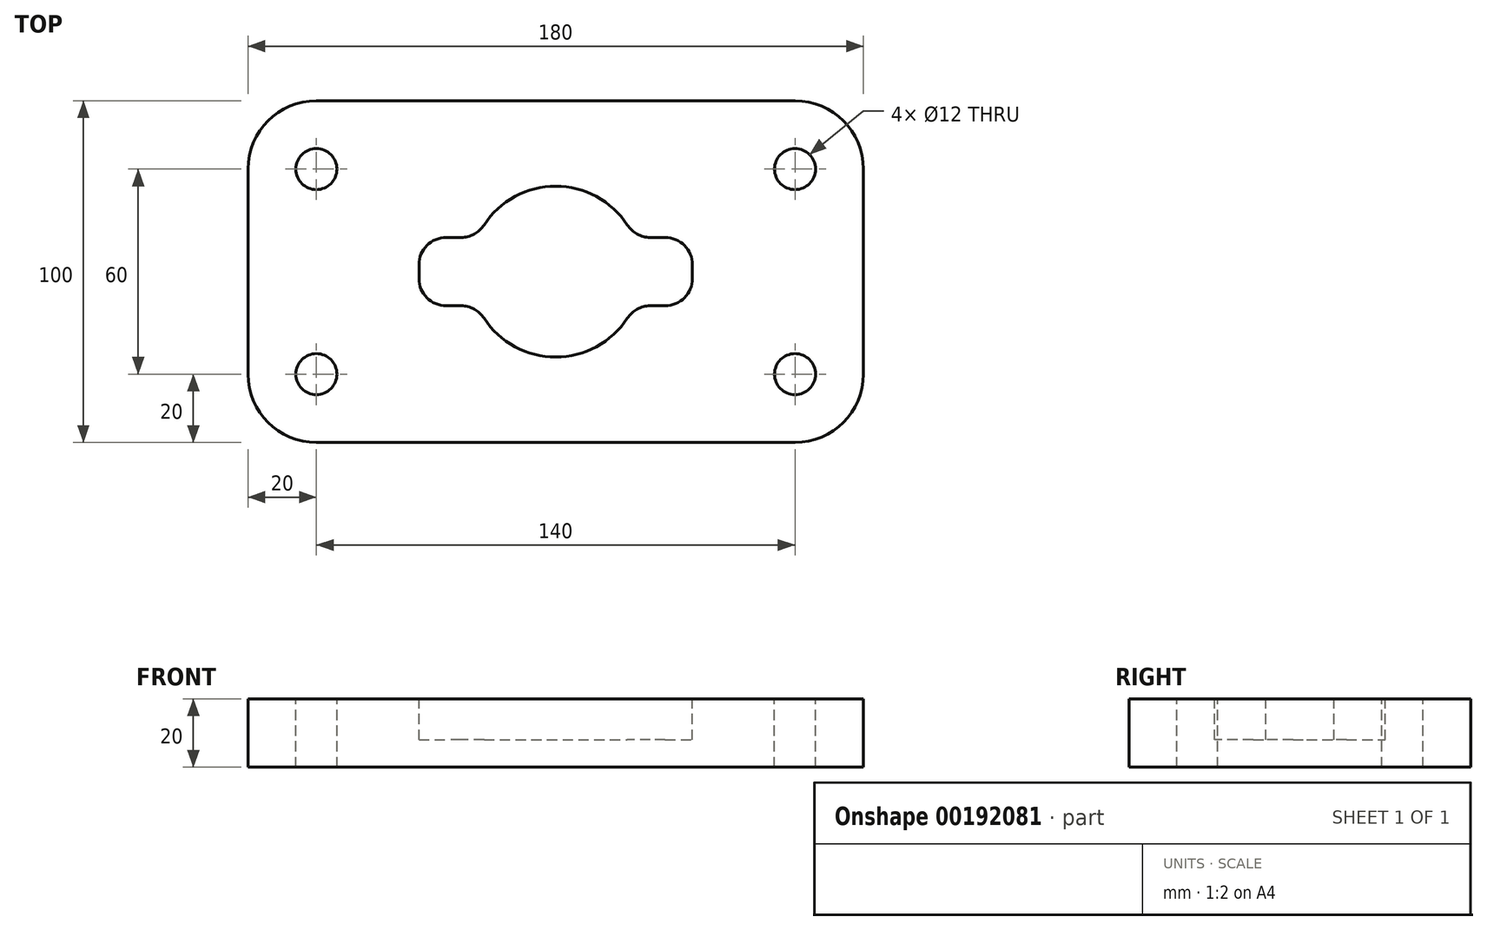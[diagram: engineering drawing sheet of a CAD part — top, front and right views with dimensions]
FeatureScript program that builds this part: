
annotation { "Feature Type Name" : "Feature", "Feature Type Description" : "" }
export const myFeature = defineFeature(function(context is Context, id is Id, definition is map)
    precondition{}
    {
        {
            var Q0;
            Q0=qCreatedBy(makeId("Top.planeOp"),FACE);
            var sketch = newSketch(context, id + "F0", { "sketchPlane" : qUnion([Q0])});
            skLineSegment(sketch, "E0.bottom", {"start": v(70, 50) * mm, "end": v(-70, 50) * mm});
            skLineSegment(sketch, "E0.top", {"start": v(70, -50) * mm, "end": v(-70, -50) * mm});
            skLineSegment(sketch, "E0.left", {"start": v(90, 30) * mm, "end": v(90, -30) * mm});
            skLineSegment(sketch, "E0.right", {"start": v(-90, 30) * mm, "end": v(-90, -30) * mm});
            skPoint(sketch, "E0.middle", {"position": v(0, 0) * mm});
            skPoint(sketch, "E1.visualSharp", {"position": v(-90, 50) * mm});
            skArc(sketch, "E1.filletArc", {"start": v(-70, 50) * mm, "mid": v(-84.14, 44.14) * mm, "end": v(-90, 30) * mm});
            skPoint(sketch, "E2.visualSharp", {"position": v(-90, -50) * mm});
            skArc(sketch, "E2.filletArc", {"start": v(-90, -30) * mm, "mid": v(-84.14, -44.14) * mm, "end": v(-70, -50) * mm});
            skPoint(sketch, "E3.visualSharp", {"position": v(90, -50) * mm});
            skArc(sketch, "E3.filletArc", {"start": v(70, -50) * mm, "mid": v(84.14, -44.14) * mm, "end": v(90, -30) * mm});
            skPoint(sketch, "E4.visualSharp", {"position": v(90, 50) * mm});
            skArc(sketch, "E4.filletArc", {"start": v(90, 30) * mm, "mid": v(84.14, 44.14) * mm, "end": v(70, 50) * mm});
            skSolve(sketch);
        }
        {
            var Q0;
            Q0 = qSketchRegion(id + "F0", true);
            extrude(context, id + "F1", {"entities" : qUnion([Q0]), "oppositeDirection" : true, "depth" : 20 * mm});
        }
        {
            var Q0;
            Q0=makeQuery(id+"F1.opExtrude","CAP_FACE",FACE,{"disambiguationData":[OSD([sQuery(id+"F0.wireOp",EDGE,"E0.bottom"),sQuery(id+"F0.wireOp",EDGE,"E0.top"),sQuery(id+"F0.wireOp",EDGE,"E0.left"),sQuery(id+"F0.wireOp",EDGE,"E0.right"),sQuery(id+"F0.wireOp",EDGE,"E1.filletArc"),sQuery(id+"F0.wireOp",EDGE,"E2.filletArc"),sQuery(id+"F0.wireOp",EDGE,"E3.filletArc"),sQuery(id+"F0.wireOp",EDGE,"E4.filletArc")])],"isStart":true});
            var sketch = newSketch(context, id + "F2", { "sketchPlane" : qUnion([Q0])});
            skCircle(sketch, "E5", {"center": v(70, 30) * mm, "radius": 6 * mm});
            skCircle(sketch, "E6", {"center": v(-70, 30) * mm, "radius": 6 * mm});
            skCircle(sketch, "E7", {"center": v(70, -30) * mm, "radius": 6 * mm});
            skCircle(sketch, "E8", {"center": v(-70, -30) * mm, "radius": 6 * mm});
            skSolve(sketch);
        }
        {
            var Q0;
            Q0 = qSketchRegion(id + "F2", true);
            extrude(context, id + "F3", {"entities" : qUnion([Q0]), "operationType" : NewBodyOperationType.REMOVE, "oppositeDirection" : true, "depth" : 25 * mm});
        }
        {
            var Q0;
            Q0=makeQuery(id+"F0.imprint","IMPRINT",FACE,{"disambiguationData":[TD([[makeQuery(id+"F0.imprint","IMPRINT",EDGE,{"derivedFrom":sQuery(id+"F0.wireOp",EDGE,"E0.bottom")}),1.0]])]});
            var sketch = newSketch(context, id + "F4", { "sketchPlane" : qUnion([Q0])});
            skLineSegment(sketch, "E9.bottom", {"start": v(32, -10) * mm, "end": v(27.66, -10) * mm});
            skLineSegment(sketch, "E9.top", {"start": v(32, 10) * mm, "end": v(27.66, 10) * mm});
            skLineSegment(sketch, "E9.left", {"start": v(40, -2) * mm, "end": v(40, 2) * mm});
            skLineSegment(sketch, "E9.right", {"start": v(-40, -2) * mm, "end": v(-40, 2) * mm});
            skPoint(sketch, "E9.middle", {"position": v(0, 0) * mm});
            skArc(sketch, "E10", {"start": v(-20.95, -13.64) * mm, "mid": v(0, -25) * mm, "end": v(20.95, -13.64) * mm});
            skLineSegment(sketch, "E11.trimOffspring", {"start": v(-27.66, 10) * mm, "end": v(-32, 10) * mm});
            skLineSegment(sketch, "E12.trimOffspring", {"start": v(-27.66, -10) * mm, "end": v(-32, -10) * mm});
            skArc(sketch, "E13.trimOffspring", {"start": v(20.95, 13.64) * mm, "mid": v(0, 25) * mm, "end": v(-20.95, 13.64) * mm});
            skPoint(sketch, "E14.visualSharp", {"position": v(22.91, -10) * mm});
            skArc(sketch, "E14.filletArc", {"start": v(27.66, -10) * mm, "mid": v(23.84, -10.97) * mm, "end": v(20.95, -13.64) * mm});
            skPoint(sketch, "E15.visualSharp", {"position": v(-22.91, -10) * mm});
            skArc(sketch, "E15.filletArc", {"start": v(-20.95, -13.64) * mm, "mid": v(-23.84, -10.97) * mm, "end": v(-27.66, -10) * mm});
            skPoint(sketch, "E16.visualSharp", {"position": v(-22.91, 10) * mm});
            skArc(sketch, "E16.filletArc", {"start": v(-27.66, 10) * mm, "mid": v(-23.84, 10.97) * mm, "end": v(-20.95, 13.64) * mm});
            skPoint(sketch, "E17.visualSharp", {"position": v(-40, 10) * mm});
            skArc(sketch, "E17.filletArc", {"start": v(-32, 10) * mm, "mid": v(-37.66, 7.66) * mm, "end": v(-40, 2) * mm});
            skPoint(sketch, "E18.visualSharp", {"position": v(-40, -10) * mm});
            skArc(sketch, "E18.filletArc", {"start": v(-40, -2) * mm, "mid": v(-37.66, -7.66) * mm, "end": v(-32, -10) * mm});
            skPoint(sketch, "E19.visualSharp", {"position": v(22.91, 10) * mm});
            skArc(sketch, "E19.filletArc", {"start": v(20.95, 13.64) * mm, "mid": v(23.84, 10.97) * mm, "end": v(27.66, 10) * mm});
            skPoint(sketch, "E20.visualSharp", {"position": v(40, -10) * mm});
            skArc(sketch, "E20.filletArc", {"start": v(32, -10) * mm, "mid": v(37.66, -7.66) * mm, "end": v(40, -2) * mm});
            skPoint(sketch, "E21.visualSharp", {"position": v(40, 10) * mm});
            skArc(sketch, "E21.filletArc", {"start": v(40, 2) * mm, "mid": v(37.66, 7.66) * mm, "end": v(32, 10) * mm});
            skSolve(sketch);
        }
        {
            var Q0;
            Q0=makeQuery(id+"F4.imprint","IMPRINT",FACE,{"disambiguationData":[TD([[makeQuery(id+"F4.imprint","IMPRINT",EDGE,{"derivedFrom":sQuery(id+"F4.wireOp",EDGE,"E9.bottom")}),-1.0]])]});
            extrude(context, id + "F5", {"entities" : qUnion([Q0]), "operationType" : NewBodyOperationType.REMOVE, "oppositeDirection" : true, "depth" : 12 * mm});
        }
    });
